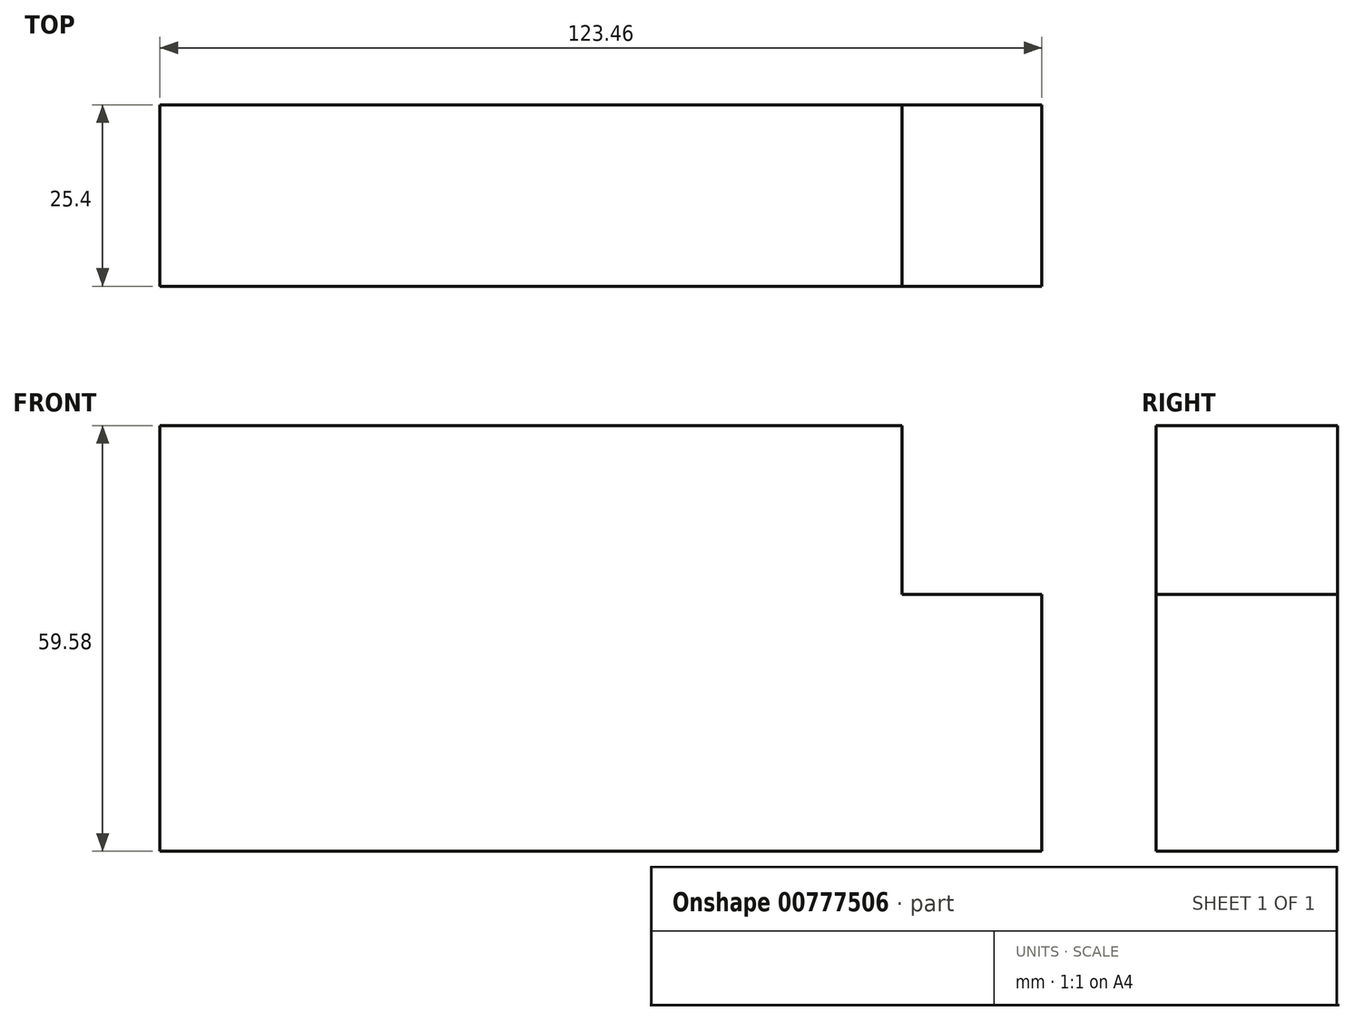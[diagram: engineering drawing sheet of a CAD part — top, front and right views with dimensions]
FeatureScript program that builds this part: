
annotation { "Feature Type Name" : "Feature", "Feature Type Description" : "" }
export const myFeature = defineFeature(function(context is Context, id is Id, definition is map)
    precondition{}
    {
        {
            var Q0;
            Q0=qCreatedBy(makeId("Front.planeOp"),FACE);
            var sketch = newSketch(context, id + "F0", { "sketchPlane" : qUnion([Q0])});
            skLineSegment(sketch, "E0.bottom", {"start": v(-49.93, 33.53) * mm, "end": v(53.96, 33.53) * mm});
            skLineSegment(sketch, "E0.top", {"start": v(-49.93, -26.05) * mm, "end": v(53.96, -26.05) * mm});
            skLineSegment(sketch, "E0.left", {"start": v(-49.93, 33.53) * mm, "end": v(-49.93, -26.05) * mm});
            skLineSegment(sketch, "E0.right", {"start": v(53.96, 33.53) * mm, "end": v(53.96, -26.05) * mm});
            skLineSegment(sketch, "E1.bottom", {"start": v(53.96, -26.05) * mm, "end": v(73.53, -26.05) * mm});
            skLineSegment(sketch, "E1.top", {"start": v(53.96, 9.93) * mm, "end": v(73.53, 9.93) * mm});
            skLineSegment(sketch, "E1.left", {"start": v(53.96, -26.05) * mm, "end": v(53.96, 9.93) * mm});
            skLineSegment(sketch, "E1.right", {"start": v(73.53, -26.05) * mm, "end": v(73.53, 9.93) * mm});
            skSolve(sketch);
        }
        {
            var Q0;
            Q0 = qSketchRegion(id + "F0", true);
            extrude(context, id + "F1", {"entities" : qUnion([Q0]), "depth" : 25.4 * mm, "offsetDistance" : 25.4 * mm});
        }
    });
